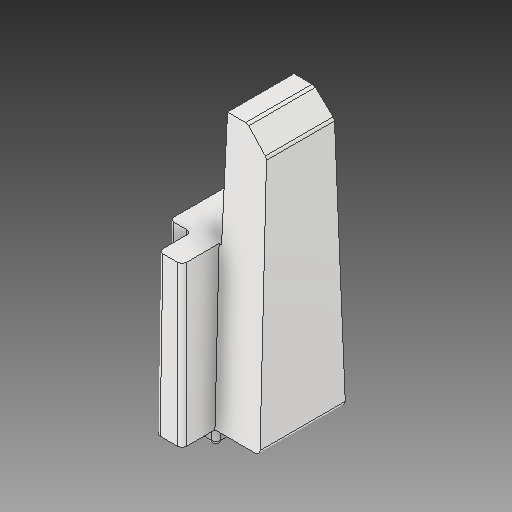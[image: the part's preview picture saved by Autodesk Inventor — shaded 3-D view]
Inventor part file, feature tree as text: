
AUTODESK INVENTOR PART (.ipt)
format: ipt  version: 2019 (Build 230136000, 136)  size: 175,616 bytes
history: native  units: in
note: dims shown in document units (in); Inventor stores cm internally (conversion verified against a paired STEP export)
features: fillet x1
ambient origin geometry x8: Origin, YZ Plane, XZ Plane, XY Plane, X Axis, Y Axis, Z Axis, Center Point
bodies: Solid1 (feature_tree)
feature tree (1):
  fillet  "Fillet4"  [1 undecoded]
note: 1 required parameter value undecoded (feature->parameter linkage not recoverable at this tier; creation-order binding heuristic only, values carry confidence <= 0.55)
